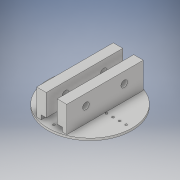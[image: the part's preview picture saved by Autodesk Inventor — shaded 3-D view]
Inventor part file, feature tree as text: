
AUTODESK INVENTOR PART (.ipt)
format: ipt  version: 2019 (Build 230136000, 136)  size: 174,592 bytes
history: native  units: mm
features: extrude x5, sketch x4, plane x2, mirror x1, projected_geometry x1
ambient origin geometry x8: Origin, YZ Plane, XZ Plane, XY Plane, X Axis, Y Axis, Z Axis, Center Point
bodies: Solid1 (feature_tree)
feature tree (13):
  extrude  "Extrusion1"  Depth=12.0mm TaperAngle=0.0deg
  extrude  "Extrusion4"  Depth=12.0mm TaperAngle=0.0deg
  sketch  "Sketch6"  dims[d21=2.375mm d22=0.0mm d23=0.0mm]
  extrude  "Extrusion5"  TaperAngle=0.0deg  [1 undecoded]
  extrude  "Extrusion6"  Depth=10.0mm TaperAngle=0.0deg
  plane  "Work Plane1"
  mirror  "Mirror1"
  plane  "Work Plane2"
  extrude  "Extrusion7"  [1 undecoded]
  sketch  "Sketch1"  dims[d0=1.0mm d1=0.0mm d15=12.0mm d16=0.0mm]
  sketch  "Sketch5"  dims[d18=3.0mm d19=12.0mm d20=0.0mm]
  sketch  "Sketch7"  dims[d24=0.0mm d33=10.0mm d34=0.0mm]
  projected_geometry  "Projected Loop2"
note: 2 required parameter values undecoded (feature->parameter linkage not recoverable at this tier; creation-order binding heuristic only, values carry confidence <= 0.55)
